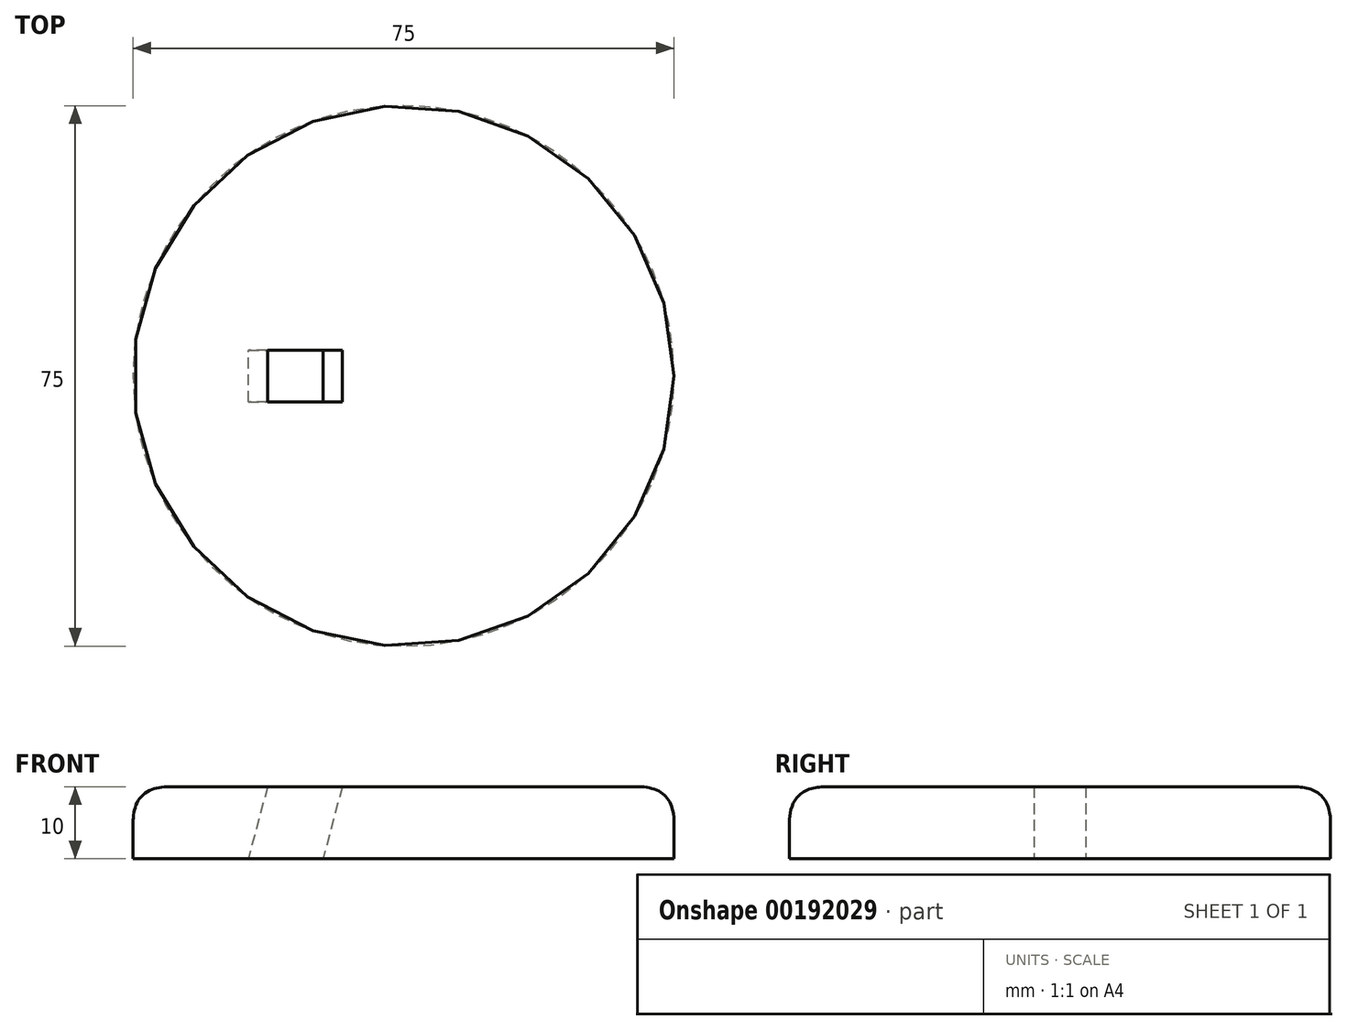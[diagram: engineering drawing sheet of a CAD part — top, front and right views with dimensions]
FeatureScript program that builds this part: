
annotation { "Feature Type Name" : "Feature", "Feature Type Description" : "" }
export const myFeature = defineFeature(function(context is Context, id is Id, definition is map)
    precondition{}
    {
        {
            var Q0;
            Q0=qCreatedBy(makeId("Top.planeOp"),FACE);
            var sketch = newSketch(context, id + "F0", { "sketchPlane" : qUnion([Q0])});
            skCircle(sketch, "E0", {"center": v(0, 0) * mm, "radius": 37.5 * mm});
            skSolve(sketch);
        }
        {
            var Q0;
            Q0=makeQuery(id+"F0.imprint","IMPRINT",FACE,{"disambiguationData":[TD([[makeQuery(id+"F0.imprint","IMPRINT",EDGE,{"derivedFrom":sQuery(id+"F0.wireOp",EDGE,"E0")}),1.0]])]});
            extrude(context, id + "F1", {"entities" : qUnion([Q0]), "depth" : 10 * mm});
        }
        {
            var Q0;
            Q0=makeQuery(id+"F1.opExtrude","CAP_FACE",FACE,{"disambiguationData":[OSD([sQuery(id+"F0.wireOp",EDGE,"E0")])],"isStart":false});
            fillet(context, id + "F2", {"entities" : qUnion([Q0]), "radius" : 5 * mm, "tangentPropagation" : true, "rho" : 0.5, "crossSection" : FilletCrossSection.CONIC, "allowEdgeOverflow" : false});
        }
        {
            var Q0;
            Q0=qCreatedBy(makeId("Front.planeOp"),FACE);
            var sketch = newSketch(context, id + "F3", { "sketchPlane" : qUnion([Q0])});
            skLineSegment(sketch, "E1.bottom", {"start": v(5, 32) * mm, "end": v(-5, 32) * mm});
            skLineSegment(sketch, "E1.top", {"start": v(5, -32) * mm, "end": v(-5, -32) * mm});
            skLineSegment(sketch, "E1.left", {"start": v(5, 32) * mm, "end": v(5, -32) * mm});
            skLineSegment(sketch, "E1.right", {"start": v(-5, 32) * mm, "end": v(-5, -32) * mm});
            skPoint(sketch, "E1.middle", {"position": v(0, 0) * mm});
            skSolve(sketch);
        }
        {
            var Q0;
            Q0=makeQuery(id+"F3.imprint","IMPRINT",FACE,{"disambiguationData":[TD([[makeQuery(id+"F3.imprint","IMPRINT",EDGE,{"derivedFrom":sQuery(id+"F3.wireOp",EDGE,"E1.bottom")}),1.0]])]});
            extrude(context, id + "F4", {"entities" : qUnion([Q0]), "endBound" : BoundingType.SYMMETRIC, "depth" : 7.15 * mm});
        }
        {
            var Q0;
            Q0=makeQuery(id+"F4.opExtrude","SWEPT_BODY",BODY,{"disambiguationData":[OSD([sQuery(id+"F3.wireOp",EDGE,"E1.bottom"),sQuery(id+"F3.wireOp",EDGE,"E1.top"),sQuery(id+"F3.wireOp",EDGE,"E1.left"),sQuery(id+"F3.wireOp",EDGE,"E1.right")])]});
            var Q1;
            Q1=makeQuery(id+"F4.opExtrude","SWEPT_EDGE",EDGE,{"disambiguationData":[OSD([sQuery(id+"F3.wireOp",EDGE,"E1.bottom"),sQuery(id+"F3.wireOp",EDGE,"E1.right")])]});
            transform(context, id + "F5", {"entities" : qUnion([Q0]), "transformType" : TransformType.ROTATION, "transformAxis" : qUnion([Q1]), "angle" : 15 * degree, "makeCopy" : false});
        }
        {
            var Q0;
            Q0=makeQuery(id+"F4.opExtrude","SWEPT_BODY",BODY,{"disambiguationData":[OSD([sQuery(id+"F3.wireOp",EDGE,"E1.bottom"),sQuery(id+"F3.wireOp",EDGE,"E1.top"),sQuery(id+"F3.wireOp",EDGE,"E1.left"),sQuery(id+"F3.wireOp",EDGE,"E1.right")])]});
            transform(context, id + "F6", {"entities" : qUnion([Q0]), "transformType" : TransformType.TRANSLATION_3D, "dx" : 0 * mm, "dy" : 0 * mm, "dz" : 29.7 * mm, "makeCopy" : false});
        }
        {
            var Q0;
            Q0=makeQuery(id+"F4.opExtrude","SWEPT_BODY",BODY,{"disambiguationData":[OSD([sQuery(id+"F3.wireOp",EDGE,"E1.bottom"),sQuery(id+"F3.wireOp",EDGE,"E1.top"),sQuery(id+"F3.wireOp",EDGE,"E1.left"),sQuery(id+"F3.wireOp",EDGE,"E1.right")])]});
            var Q1;
            Q1=makeQuery(id+"F1.opExtrude","SWEPT_BODY",BODY,{"disambiguationData":[OSD([sQuery(id+"F0.wireOp",EDGE,"E0")])]});
            booleanBodies(context, id + "F7", {"operationType" : BooleanOperationType.SUBTRACTION, "tools" : qUnion([Q0]), "targets" : qUnion([Q1])});
        }
    });
